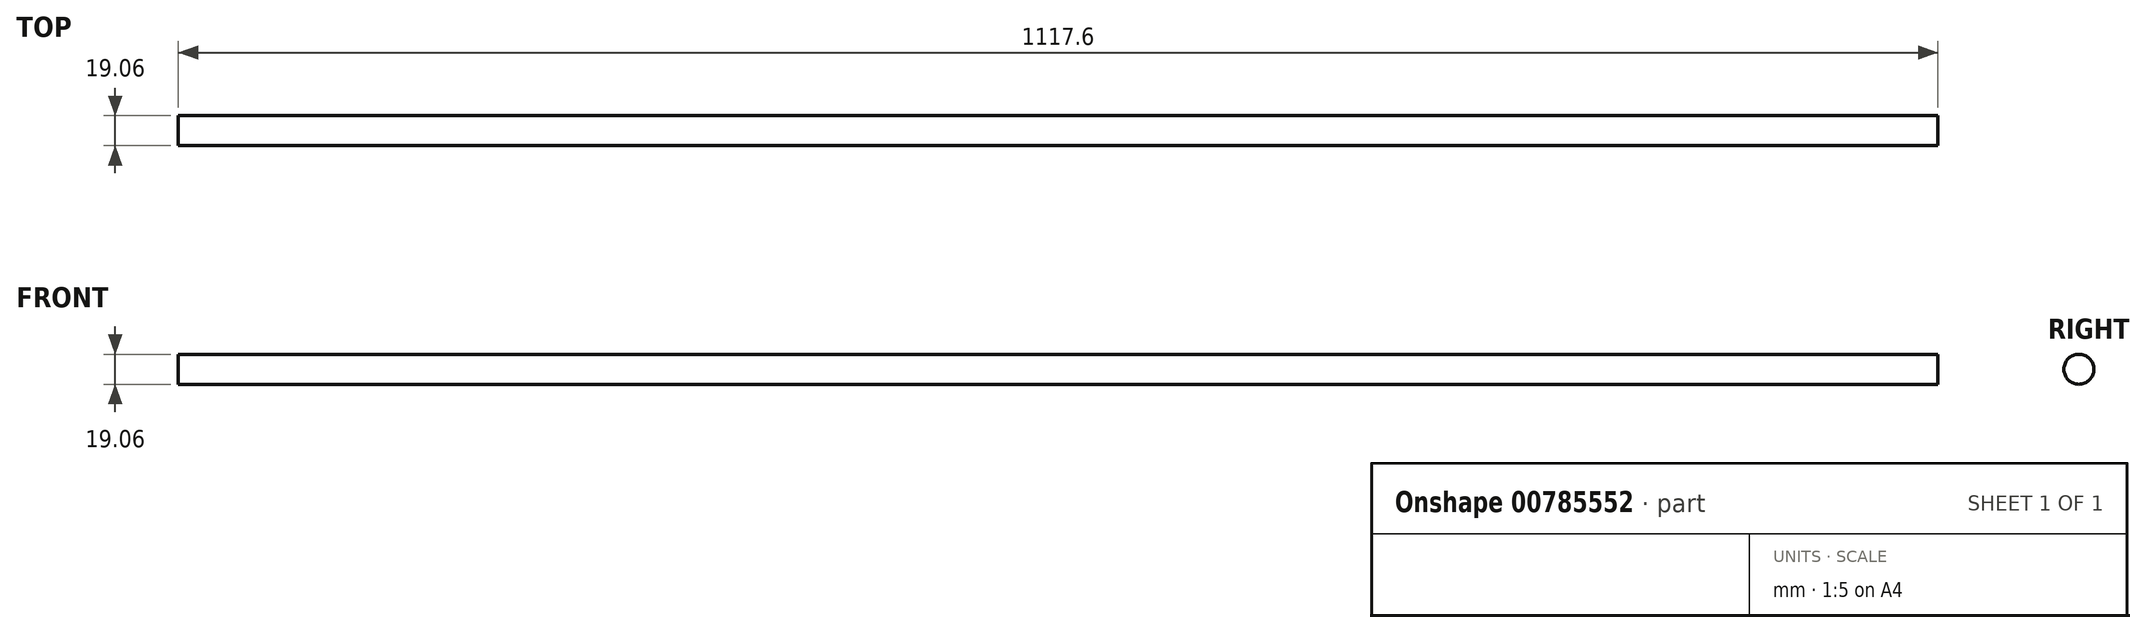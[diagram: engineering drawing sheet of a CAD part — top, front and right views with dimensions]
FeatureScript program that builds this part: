
annotation { "Feature Type Name" : "Feature", "Feature Type Description" : "" }
export const myFeature = defineFeature(function(context is Context, id is Id, definition is map)
    precondition{}
    {
        {
            var Q0;
            Q0=qCreatedBy(makeId("Right.planeOp"),FACE);
            var sketch = newSketch(context, id + "F0", { "sketchPlane" : qUnion([Q0])});
            skCircle(sketch, "E0", {"center": v(0, 0) * mm, "radius": 9.53 * mm});
            skSolve(sketch);
        }
        {
            var Q0;
            Q0 = qSketchRegion(id + "F0", true);
            extrude(context, id + "F1", {"entities" : qUnion([Q0]), "depth" : 1117.6 * mm, "offsetDistance" : 25.4 * mm});
        }
    });
